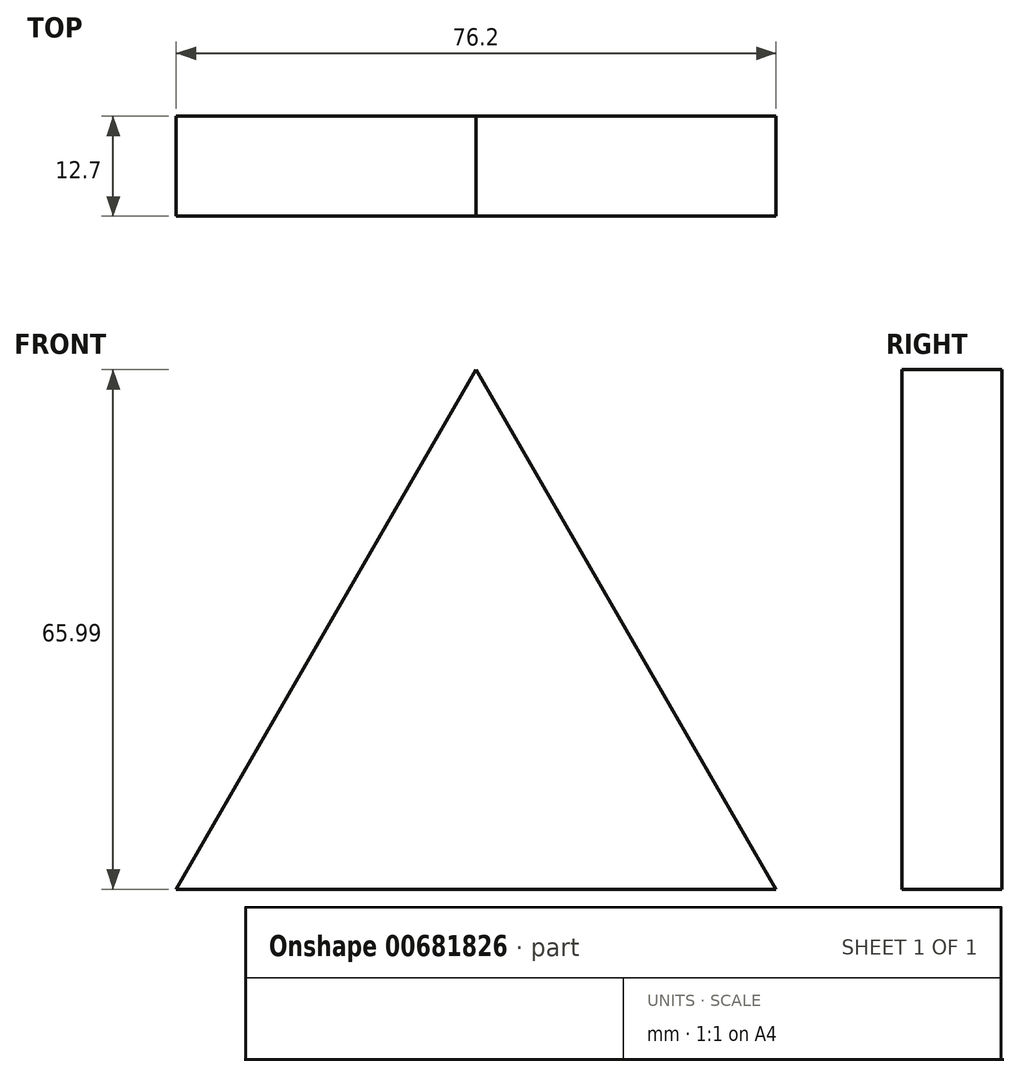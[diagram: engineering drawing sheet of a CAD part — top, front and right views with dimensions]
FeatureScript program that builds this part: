
annotation { "Feature Type Name" : "Feature", "Feature Type Description" : "" }
export const myFeature = defineFeature(function(context is Context, id is Id, definition is map)
    precondition{}
    {
        {
            var Q0;
            Q0=qCreatedBy(makeId("Front.planeOp"),FACE);
            var sketch = newSketch(context, id + "F0", { "sketchPlane" : qUnion([Q0])});
            skPoint(sketch, "E0.start.orphan", {"position": v(-76.54, 0) * mm});
            skLineSegment(sketch, "E1", {"start": v(-19.5, 66) * mm, "end": v(18.6, 0) * mm});
            skLineSegment(sketch, "E2", {"start": v(18.6, 0) * mm, "end": v(-57.6, 0) * mm});
            skLineSegment(sketch, "E3", {"start": v(-57.6, 0) * mm, "end": v(-19.5, 66) * mm});
            skSolve(sketch);
        }
        {
            var Q0;
            Q0=makeQuery(id+"F0.imprint","IMPRINT",FACE,{"disambiguationData":[TD([[makeQuery(id+"F0.imprint","IMPRINT",EDGE,{"derivedFrom":sQuery(id+"F0.wireOp",EDGE,"E1")}),-1.0]])]});
            extrude(context, id + "F1", {"entities" : qUnion([Q0]), "depth" : 12.7 * mm, "offsetDistance" : 25.4 * mm});
        }
    });
